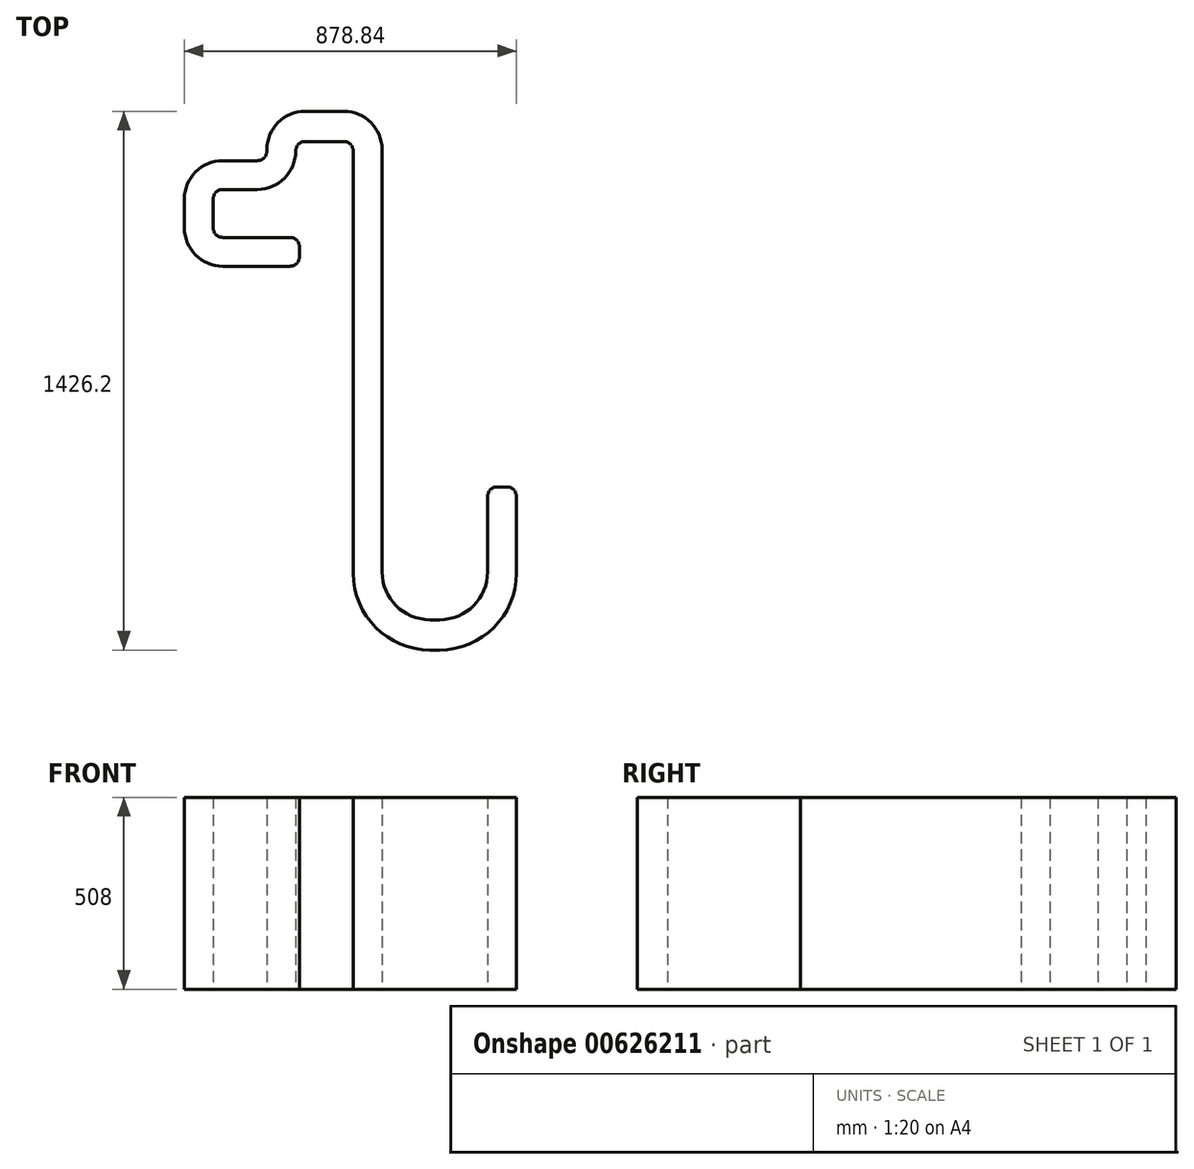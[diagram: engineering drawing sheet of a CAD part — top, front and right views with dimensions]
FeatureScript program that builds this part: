
annotation { "Feature Type Name" : "Feature", "Feature Type Description" : "" }
export const myFeature = defineFeature(function(context is Context, id is Id, definition is map)
    precondition{}
    {
        {
            var Q0;
            Q0=qCreatedBy(makeId("Top.planeOp"),FACE);
            var sketch = newSketch(context, id + "F0", { "sketchPlane" : qUnion([Q0])});
            skLineSegment(sketch, "E0", {"start": v(-25.4, 0) * mm, "end": v(-203.2, 0) * mm});
            skLineSegment(sketch, "E1", {"start": v(-228.6, 25.4) * mm, "end": v(-228.6, 101.6) * mm});
            skLineSegment(sketch, "E2", {"start": v(-203.2, 127) * mm, "end": v(-111.76, 127) * mm});
            skLineSegment(sketch, "E3", {"start": v(-10.16, 228.6) * mm, "end": v(-10.16, 228.6) * mm});
            skLineSegment(sketch, "E4", {"start": v(15.24, 254) * mm, "end": v(116.84, 254) * mm});
            skLineSegment(sketch, "E5", {"start": v(142.24, 228.6) * mm, "end": v(142.24, -889) * mm});
            skLineSegment(sketch, "E6", {"start": v(345.44, -1092.2) * mm, "end": v(370.84, -1092.2) * mm});
            skLineSegment(sketch, "E7", {"start": v(574.04, -889) * mm, "end": v(574.04, -685.8) * mm});
            skLineSegment(sketch, "E8", {"start": v(548.64, -660.4) * mm, "end": v(523.24, -660.4) * mm});
            skLineSegment(sketch, "E9", {"start": v(497.84, -685.8) * mm, "end": v(497.84, -885.2) * mm});
            skLineSegment(sketch, "E10", {"start": v(370.84, -1012.2) * mm, "end": v(345.44, -1012.2) * mm});
            skLineSegment(sketch, "E11", {"start": v(218.44, -885.2) * mm, "end": v(218.44, 232.4) * mm});
            skLineSegment(sketch, "E12", {"start": v(116.84, 334) * mm, "end": v(15.24, 334) * mm});
            skLineSegment(sketch, "E13", {"start": v(-86.36, 232.4) * mm, "end": v(-86.36, 228.6) * mm});
            skLineSegment(sketch, "E14", {"start": v(-111.76, 203.2) * mm, "end": v(-203.2, 203.2) * mm});
            skLineSegment(sketch, "E15", {"start": v(-304.8, 101.6) * mm, "end": v(-304.8, 25.4) * mm});
            skLineSegment(sketch, "E16", {"start": v(-203.2, -76.2) * mm, "end": v(-25.4, -76.2) * mm});
            skLineSegment(sketch, "E17", {"start": v(0, -50.8) * mm, "end": v(0, -25.4) * mm});
            skPoint(sketch, "E18.visualSharp", {"position": v(-304.8, 203.2) * mm});
            skArc(sketch, "E18.filletArc", {"start": v(-203.2, 203.2) * mm, "mid": v(-275.04, 173.44) * mm, "end": v(-304.8, 101.6) * mm});
            skPoint(sketch, "E19.visualSharp", {"position": v(-86.36, 334) * mm});
            skArc(sketch, "E19.filletArc", {"start": v(15.24, 334) * mm, "mid": v(-56.6, 304.25) * mm, "end": v(-86.36, 232.4) * mm});
            skPoint(sketch, "E20.visualSharp", {"position": v(218.44, 334) * mm});
            skArc(sketch, "E20.filletArc", {"start": v(218.44, 232.4) * mm, "mid": v(188.68, 304.25) * mm, "end": v(116.84, 334) * mm});
            skPoint(sketch, "E21.visualSharp", {"position": v(-10.16, 127) * mm});
            skArc(sketch, "E21.filletArc", {"start": v(-111.76, 127) * mm, "mid": v(-39.92, 156.76) * mm, "end": v(-10.16, 228.6) * mm});
            skPoint(sketch, "E22.visualSharp", {"position": v(-228.6, 127) * mm});
            skArc(sketch, "E22.filletArc", {"start": v(-203.2, 127) * mm, "mid": v(-221.16, 119.56) * mm, "end": v(-228.6, 101.6) * mm});
            skPoint(sketch, "E23.visualSharp", {"position": v(-86.36, 203.2) * mm});
            skArc(sketch, "E23.filletArc", {"start": v(-111.76, 203.2) * mm, "mid": v(-93.8, 210.64) * mm, "end": v(-86.36, 228.6) * mm});
            skPoint(sketch, "E24.visualSharp", {"position": v(-228.6, 0) * mm});
            skArc(sketch, "E24.filletArc", {"start": v(-228.6, 25.4) * mm, "mid": v(-221.16, 7.44) * mm, "end": v(-203.2, 0) * mm});
            skPoint(sketch, "E25.visualSharp", {"position": v(0, 0) * mm});
            skArc(sketch, "E25.filletArc", {"start": v(0, -25.4) * mm, "mid": v(-7.44, -7.44) * mm, "end": v(-25.4, 0) * mm});
            skPoint(sketch, "E26.visualSharp", {"position": v(0, -76.2) * mm});
            skArc(sketch, "E26.filletArc", {"start": v(-25.4, -76.2) * mm, "mid": v(-7.44, -68.76) * mm, "end": v(0, -50.8) * mm});
            skPoint(sketch, "E27.visualSharp", {"position": v(-304.8, -76.2) * mm});
            skArc(sketch, "E27.filletArc", {"start": v(-304.8, 25.4) * mm, "mid": v(-275.04, -46.44) * mm, "end": v(-203.2, -76.2) * mm});
            skPoint(sketch, "E28.visualSharp", {"position": v(-10.16, 254) * mm});
            skArc(sketch, "E28.filletArc", {"start": v(15.24, 254) * mm, "mid": v(-2.72, 246.56) * mm, "end": v(-10.16, 228.6) * mm});
            skPoint(sketch, "E29.visualSharp", {"position": v(142.24, 254) * mm});
            skArc(sketch, "E29.filletArc", {"start": v(142.24, 228.6) * mm, "mid": v(134.8, 246.56) * mm, "end": v(116.84, 254) * mm});
            skPoint(sketch, "E30.visualSharp", {"position": v(218.44, -1012.2) * mm});
            skArc(sketch, "E30.filletArc", {"start": v(218.44, -885.2) * mm, "mid": v(255.64, -975) * mm, "end": v(345.44, -1012.2) * mm});
            skPoint(sketch, "E31.visualSharp", {"position": v(497.84, -1012.2) * mm});
            skArc(sketch, "E31.filletArc", {"start": v(370.84, -1012.2) * mm, "mid": v(460.64, -975) * mm, "end": v(497.84, -885.2) * mm});
            skPoint(sketch, "E32.visualSharp", {"position": v(497.84, -660.4) * mm});
            skArc(sketch, "E32.filletArc", {"start": v(523.24, -660.4) * mm, "mid": v(505.28, -667.84) * mm, "end": v(497.84, -685.8) * mm});
            skPoint(sketch, "E33.visualSharp", {"position": v(574.04, -660.4) * mm});
            skArc(sketch, "E33.filletArc", {"start": v(574.04, -685.8) * mm, "mid": v(566.6, -667.84) * mm, "end": v(548.64, -660.4) * mm});
            skPoint(sketch, "E34.visualSharp", {"position": v(574.04, -1092.2) * mm});
            skArc(sketch, "E34.filletArc", {"start": v(370.84, -1092.2) * mm, "mid": v(514.52, -1032.68) * mm, "end": v(574.04, -889) * mm});
            skPoint(sketch, "E35.visualSharp", {"position": v(142.24, -1092.2) * mm});
            skArc(sketch, "E35.filletArc", {"start": v(142.24, -889) * mm, "mid": v(201.76, -1032.68) * mm, "end": v(345.44, -1092.2) * mm});
            skSolve(sketch);
        }
        {
            var Q0;
            Q0 = qSketchRegion(id + "F0", true);
            extrude(context, id + "F1", {"entities" : qUnion([Q0]), "depth" : 508 * mm, "offsetDistance" : 25.4 * mm});
        }
    });
